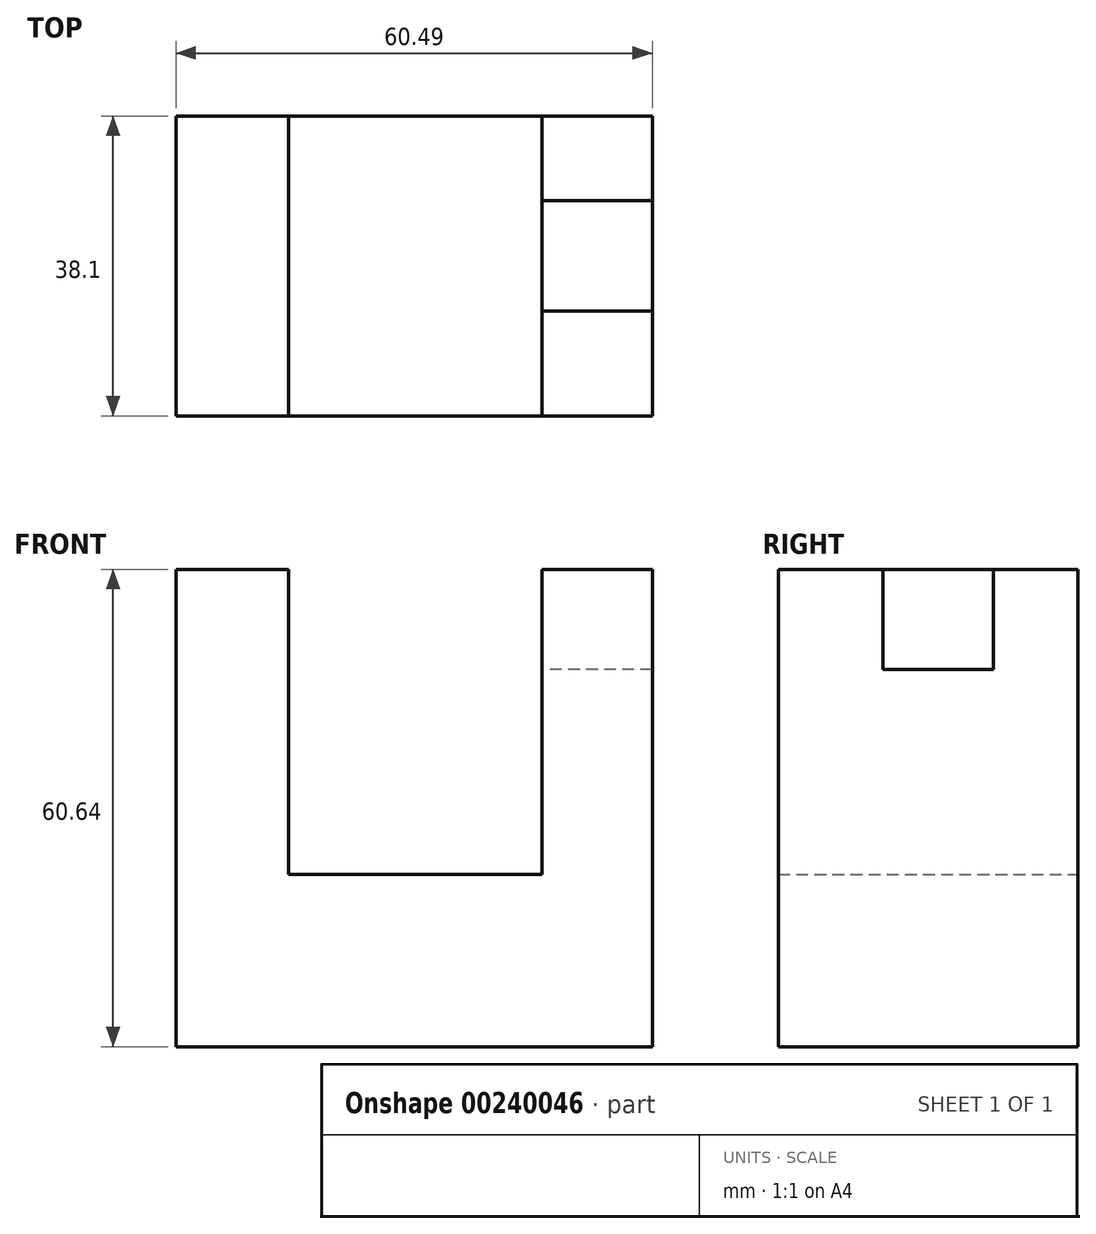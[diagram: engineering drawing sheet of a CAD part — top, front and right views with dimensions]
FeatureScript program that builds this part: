
annotation { "Feature Type Name" : "Feature", "Feature Type Description" : "" }
export const myFeature = defineFeature(function(context is Context, id is Id, definition is map)
    precondition{}
    {
        {
            var Q0;
            Q0=qCreatedBy(makeId("Front.planeOp"),FACE);
            var sketch = newSketch(context, id + "F0", { "sketchPlane" : qUnion([Q0])});
            skLineSegment(sketch, "E0.bottom", {"start": v(0, 0) * mm, "end": v(60.5, 0) * mm});
            skLineSegment(sketch, "E0.top", {"start": v(0, 60.64) * mm, "end": v(14.3, 60.64) * mm});
            skLineSegment(sketch, "E0.left", {"start": v(0, 0) * mm, "end": v(0, 60.64) * mm});
            skLineSegment(sketch, "E0.right", {"start": v(60.5, 0) * mm, "end": v(60.5, 60.64) * mm});
            skLineSegment(sketch, "E1", {"start": v(14.3, 60.64) * mm, "end": v(14.3, 21.9) * mm});
            skLineSegment(sketch, "E2", {"start": v(14.3, 21.9) * mm, "end": v(46.49, 21.9) * mm});
            skLineSegment(sketch, "E3", {"start": v(46.49, 21.9) * mm, "end": v(46.49, 60.64) * mm});
            skLineSegment(sketch, "E4", {"start": v(46.49, 60.64) * mm, "end": v(60.5, 60.64) * mm});
            skSolve(sketch);
        }
        {
            var Q0;
            Q0=makeQuery(id+"F0.imprint","IMPRINT",FACE,{"disambiguationData":[TD([[makeQuery(id+"F0.imprint","IMPRINT",EDGE,{"derivedFrom":sQuery(id+"F0.wireOp",EDGE,"E0.bottom")}),1.0]])]});
            extrude(context, id + "F1", {"entities" : qUnion([Q0]), "depth" : 38.1 * mm});
        }
        {
            var Q0;
            Q0=makeQuery(id+"F1.opExtrude","SWEPT_FACE",FACE,{"disambiguationData":[OSD([sQuery(id+"F0.wireOp",EDGE,"E4")])]});
            var sketch = newSketch(context, id + "F2", { "sketchPlane" : qUnion([Q0])});
            skLineSegment(sketch, "E5", {"start": v(60.5, -24.77) * mm, "end": v(46.49, -24.77) * mm});
            skPoint(sketch, "E5.endSnap0", {"position": v(46.49, -19.05) * mm});
            skLineSegment(sketch, "E6", {"start": v(46.49, -24.77) * mm, "end": v(46.49, -10.77) * mm});
            skLineSegment(sketch, "E7", {"start": v(46.49, -10.77) * mm, "end": v(60.5, -10.77) * mm});
            skLineSegment(sketch, "E8", {"start": v(60.5, -10.77) * mm, "end": v(60.5, -24.77) * mm});
            skSolve(sketch);
        }
        {
            var Q0;
            Q0=makeQuery(id+"F2.imprint","IMPRINT",FACE,{"disambiguationData":[TD([[makeQuery(id+"F2.imprint","IMPRINT",EDGE,{"derivedFrom":sQuery(id+"F2.wireOp",EDGE,"E5")}),-1.0]])]});
            extrude(context, id + "F3", {"entities" : qUnion([Q0]), "operationType" : NewBodyOperationType.REMOVE, "oppositeDirection" : true, "depth" : 12.7 * mm});
        }
    });
